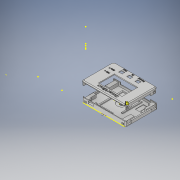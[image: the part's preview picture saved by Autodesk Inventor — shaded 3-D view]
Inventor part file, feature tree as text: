
AUTODESK INVENTOR PART (.ipt)
format: ipt  version: 2019 (Build 230136000, 136)  size: 3,585,536 bytes
history: native  units: mm
features: move_body x109, sketch x92, extrude x72, direct_edit x59, chamfer x6, other x3, split x1, draft x1, revolve x1, plane x1
ambient origin geometry x8: Origin, YZ Plane, XZ Plane, XY Plane, X Axis, Y Axis, Z Axis, Center Point
bodies: Solid1 (feature_tree), Solid2 (feature_tree), Solid3 (feature_tree)
feature tree (345):
  sketch  "Sketch1"  dims[d2=105.0mm d3=75.0mm d6=109.0mm]
  extrude  "Extrusion1"  Depth=109.0mm
  extrude  "Extrusion2"  Depth=79.0mm TaperAngle=0.0deg
  extrude  "Extrusion3"  Depth=2.5mm TaperAngle=0.0deg
  sketch  "Sketch6"  dims[d10=105.0mm d11=75.0mm d12=2.5mm d13=0.0mm]
  extrude  "Extrusion4"  Depth=19.5mm
  sketch  "Sketch8"  dims[d17=10.0mm d18=1.2mm d19=0.0mm]
  extrude  "Extrusion5"  Depth=10.0mm TaperAngle=0.0deg
  extrude  "Extrusion6"  Depth=30.0mm
  extrude  "Extrusion7"  Depth=60.0mm
  extrude  "Extrusion8"  Depth=1.0mm TaperAngle=0.0deg
  sketch  "Sketch14"  dims[d31=2.8mm d32=60.0mm]
  extrude  "Extrusion9"  Depth=20.0mm
  extrude  "Extrusion10"  Depth=0.5mm TaperAngle=0.0deg
  extrude  "Extrusion11"  Depth=12.5mm
  extrude  "Extrusion12"  Depth=10.0mm TaperAngle=0.0deg
  sketch  "Sketch17"  dims[d33=5.6mm d34=1.0mm d35=0.0mm]
  sketch  "Sketch18"  dims[d36=16.0mm d37=20.0mm]
  sketch  "Sketch19"  dims[d38=1.0mm d39=0.0mm d40=0.5mm d41=0.0mm]
  sketch  "Sketch20"  dims[d42=11.0mm d43=12.5mm]
  sketch  "Sketch21"  dims[d44=10.0mm d45=1.0mm d46=0.0mm]
  extrude  "Extrusion13"  Depth=2.0mm TaperAngle=0.0deg
  extrude  "Extrusion14"  Depth=15.0mm
  sketch  "Sketch22"  dims[d47=0.2mm d48=0.0mm d49=2.0mm d50=0.0mm]
  direct_edit  "Direct Edit1"
  direct_edit  "Direct Edit2"
  extrude  "Extrusion15"  Depth=70.0mm
  extrude  "Extrusion16"  Depth=58.0mm
  extrude  "Extrusion17"  Depth=2.0mm TaperAngle=0.0deg
  direct_edit  "Direct Edit3"
  direct_edit  "Direct Edit4"
  direct_edit  "Direct Edit5"
  extrude  "Extrusion18"  Depth=79.0mm
  extrude  "Extrusion19"  TaperAngle=0.0deg  [1 undecoded]
  extrude  "Extrusion20"  Depth=3.0mm TaperAngle=0.0deg
  extrude  "Extrusion21"  Depth=3.0mm
  direct_edit  "Direct Edit6"
  split  "Split1"
  move_body  "Move Body1"
  move_body  "Move Body2"
  move_body  "Move Body3"
  move_body  "Move Body4"
  move_body  "Move Body5"
  move_body  "Move Body6"
  sketch  "Sketch28"  dims[d63=2.5mm d64=0.0mm d65=0.0mm d66=0.0mm d67=-0.5mm]
  direct_edit  "Direct Edit7"
  sketch  "Sketch29"  dims[d68=0.0mm d69=0.0mm d70=1.0mm d71=3.0mm d72=0.0mm]
  extrude  "Extrusion22"  Depth=2.54mm
  extrude  "Extrusion23"  Depth=5.588mm
  sketch  "Sketch32"  dims[d84=11.176mm d85=5.588mm]
  direct_edit  "Direct Edit8"
  direct_edit  "Direct Edit9"
  extrude  "Extrusion24"  TaperAngle=0.0deg  [1 undecoded]
  direct_edit  "Direct Edit10"
  direct_edit  "Direct Edit11"
  direct_edit  "Direct Edit12"
  sketch  "Sketch33"  dims[d86=1.0mm d87=0.0mm d88=0.0mm d89=0.0mm d90=-47.25mm]
  direct_edit  "Direct Edit13"
  other  "Work Point1"
  sketch  "Sketch34"  dims[d91=0.0mm d92=0.0mm d93=-95.5mm d94=0.0mm d95=0.0mm d96=-0.6mm]
  other  "Work Point2"
  other  "Work Point3"
  sketch  "Sketch35"  dims[d101=27.7mm d102=48.2mm]
  extrude  "Extrusion25"  TaperAngle=0.0deg  [1 undecoded]
  extrude  "Extrusion26"  Depth=48.2mm
  direct_edit  "Direct Edit14"
  direct_edit  "Direct Edit15"
  extrude  "Extrusion27"  Depth=7.0mm
  extrude  "Extrusion28"  Depth=7.0mm
  direct_edit  "Direct Edit16"
  draft  "FaceDraft1"
  chamfer  "Chamfer1"  Distance=4.0mm
  chamfer  "Chamfer2"  Distance=3.0mm
  chamfer  "Chamfer3"  Distance=1.0mm
  direct_edit  "Direct Edit17"
  direct_edit  "Direct Edit18"
  extrude  "Extrusion29"  Depth=1.5mm TaperAngle=0.0deg
  extrude  "Extrusion30"  TaperAngle=0.0deg  [1 undecoded]
  extrude  "Extrusion31"  TaperAngle=180.0deg  [1 undecoded]
  sketch  "Sketch42"  dims[d121=9.75mm d122=12.75mm d123=244.0mm d124=-9.75mm d125=0.0mm d126=0.0mm]
  direct_edit  "Direct Edit19"
  sketch  "Sketch43"  dims[d127=180.0deg d128=180.0deg]
  direct_edit  "Direct Edit20"
  sketch  "Sketch44"  dims[d129=180.0deg d130=122.75mm d131=-19.25mm d132=0.0mm]
  extrude  "Extrusion32"  Depth=122.75mm TaperAngle=0.0deg
  direct_edit  "Direct Edit21"
  extrude  "Extrusion33"  Depth=5.0mm
  extrude  "Extrusion34"  Depth=5.0mm
  sketch  "Sketch48"  dims[d141=5.0mm d142=5.0mm]
  sketch  "Sketch49"  dims[d143=5.0mm d144=2.0mm]
  extrude  "Extrusion35"  Depth=5.0mm
  sketch  "Sketch51"  dims[d147=2.0mm d148=1.0mm d149=0.0mm]
  extrude  "Extrusion36"  Depth=5.0mm
  extrude  "Extrusion37"  Depth=2.0mm
  move_body  "Move Body7"
  move_body  "Move Body8"
  move_body  "Move Body9"
  move_body  "Move Body10"
  move_body  "Move Body11"
  move_body  "Move Body12"
  sketch  "Sketch53"  dims[d152=5.0mm d153=5.0mm]
  direct_edit  "Direct Edit22"
  extrude  "Extrusion38"  Depth=2.0mm
  sketch  "Sketch54"  dims[d154=5.0mm d155=5.0mm]
  sketch  "Sketch55"  dims[d156=5.0mm d157=5.0mm]
  sketch  "Sketch56"  dims[d158=3.0mm d159=3.0mm]
  extrude  "Extrusion39"  Depth=1.0mm TaperAngle=0.0deg
  direct_edit  "Direct Edit23"
  sketch  "Sketch58"  dims[d162=3.0mm d163=0.0mm d164=11.0mm]
  direct_edit  "Direct Edit24"
  extrude  "Extrusion40"  Depth=5.0mm
  direct_edit  "Direct Edit25"
  extrude  "Extrusion41"  Depth=5.0mm
  direct_edit  "Direct Edit26"
  direct_edit  "Direct Edit27"
  direct_edit  "Direct Edit28"
  direct_edit  "Direct Edit29"
  extrude  "Extrusion42"  Depth=5.0mm
  extrude  "Extrusion43"  Depth=5.0mm
  direct_edit  "Direct Edit30"
  sketch  "Sketch62"  dims[d171=11.0mm d172=0.0mm d173=0.0mm d174=1.0mm]
  extrude  "Extrusion44"  Depth=3.0mm
  direct_edit  "Direct Edit31"
  direct_edit  "Direct Edit32"
  extrude  "Extrusion45"  Depth=3.0mm
  move_body  "Move Body13"
  move_body  "Move Body14"
  move_body  "Move Body15"
  move_body  "Move Body16"
  extrude  "Extrusion46"  Depth=3.0mm
  sketch  "Sketch66"  dims[d192=0.0mm d193=0.0mm d194=1.0mm d195=12.5mm]
  direct_edit  "Direct Edit33"
  sketch  "Sketch67"  dims[d196=5.0mm d198=2.1mm]
  direct_edit  "Direct Edit34"
  extrude  "Extrusion47"  Depth=11.0mm
  direct_edit  "Direct Edit35"
  move_body  "Move Body17"
  direct_edit  "Direct Edit36"
  direct_edit  "Direct Edit37"
  direct_edit  "Direct Edit38"
  direct_edit  "Direct Edit39"
  direct_edit  "Direct Edit40"
  direct_edit  "Direct Edit41"
  extrude  "Extrusion48"  Depth=11.0mm
  extrude  "Extrusion49"  Depth=11.0mm
  extrude  "Extrusion50"  Depth=1.0mm TaperAngle=0.0deg
  sketch  "Sketch72"  dims[d213=5.0mm d214=0.0mm d215=0.6mm]
  revolve  "Revolution1"  [1 undecoded]
  sketch  "Sketch74"  dims[d218=5.0mm d219=0.0mm d220=0.0mm d221=0.0mm d222=-0.2mm]
  sketch  "Sketch75"  dims[d223=0.0mm d224=0.0mm d225=0.2mm d226=30.0deg]
  plane  "Work Plane1"
  extrude  "Extrusion51"  Depth=1.0mm TaperAngle=0.0deg
  direct_edit  "Direct Edit42"
  sketch  "Sketch77"  dims[d233=1.07845mm d234=2.0mm d235=45.0deg d236=0.0mm d237=0.0mm d238=-0.5mm]
  extrude  "Extrusion52"  TaperAngle=0.0deg  [1 undecoded]
  extrude  "Extrusion53"  Depth=12.5mm
  extrude  "Extrusion54"  Depth=2.1mm
  extrude  "Extrusion55"  Depth=10.0mm
  direct_edit  "Direct Edit43"
  direct_edit  "Direct Edit44"
  extrude  "Extrusion56"  TaperAngle=0.0deg  [1 undecoded]
  extrude  "Extrusion57"  Depth=0.6mm
  extrude  "Extrusion58"  Depth=3.05mm
  extrude  "Extrusion59"  Depth=0.6mm
  extrude  "Extrusion60"  Depth=13.7mm
  extrude  "Extrusion61"  TaperAngle=0.0deg  [1 undecoded]
  direct_edit  "Direct Edit45"
  direct_edit  "Direct Edit46"
  direct_edit  "Direct Edit47"
  extrude  "Extrusion62"  TaperAngle=30.0deg  [1 undecoded]
  direct_edit  "Direct Edit48"
  sketch  "Sketch89"  dims[d283=4.75mm d284=0.0mm d285=-118.0mm]
  extrude  "Extrusion63"  Depth=0.8mm TaperAngle=45.0deg
  extrude  "Extrusion64"  TaperAngle=0.0deg  [1 undecoded]
  extrude  "Extrusion65"  Depth=0.6mm TaperAngle=0.0deg
  extrude  "Extrusion66"  Depth=7.5mm
  extrude  "Extrusion67"  Depth=17.5mm
  sketch  "Sketch95"  dims[d299=17.8mm]
  sketch  "Sketch96"  dims[d300=20.6mm]
  extrude  "Extrusion68"  Depth=1.0mm TaperAngle=0.0deg
  direct_edit  "Direct Edit49"
  direct_edit  "Direct Edit50"
  direct_edit  "Direct Edit51"
  extrude  "Extrusion69"  Depth=3.0mm
  extrude  "Extrusion70"  Depth=1.2mm TaperAngle=0.0deg
  direct_edit  "Direct Edit52"
  extrude  "Extrusion71"  Depth=2.0mm TaperAngle=0.0deg
  direct_edit  "Direct Edit53"
  direct_edit  "Direct Edit54"
  sketch  "Sketch100"  dims[d307=13.0mm]
  extrude  "Extrusion72"  Depth=23.0mm
  direct_edit  "Direct Edit55"
  direct_edit  "Direct Edit56"
  direct_edit  "Direct Edit57"
  direct_edit  "Direct Edit58"
  direct_edit  "Direct Edit59"
  chamfer  "Chamfer4"  Distance=1.2mm
  chamfer  "Chamfer5"  Distance=1.0mm
  chamfer  "Chamfer6"  Distance=2.0mm
  sketch  "Sketch5"  dims[d7=79.0mm d8=7.0mm d9=0.0mm]
  sketch  "Sketch7"  dims[d14=5.0mm d15=0.0mm d16=19.5mm]
  sketch  "Sketch11"  dims[d28=1.0mm d29=0.0mm d30=30.0mm]
  sketch  "Sketch23"  dims[d51=2.0mm d52=0.0mm d53=15.0mm]
  sketch  "Sketch24"  dims[d54=9.0mm d55=70.0mm]
  sketch  "Sketch25"  dims[d56=46.5mm d57=58.0mm]
  sketch  "Sketch26"  dims[d58=39.0mm d59=2.0mm d60=0.0mm]
  sketch  "Sketch27"  dims[d61=109.0mm d62=79.0mm]
  sketch  "Sketch30"  dims[d73=1.0mm d74=0.0mm d79=3.0mm]
  sketch  "Sketch31"  dims[d82=4.5mm d83=2.54mm]
  sketch  "Sketch36"  dims[d103=68.2mm d104=7.0mm]
  sketch  "Sketch37"  dims[d105=5.5mm d106=7.0mm]
  sketch  "Sketch38"  dims[d107=5.5mm]
  sketch  "Sketch39"  dims[d108=7.0mm]
  sketch  "Sketch40"  dims[d109=5.5mm d110=4.0mm d111=0.0mm d112=3.0mm d113=0.0mm d114=1.0mm d115=0.0mm]
  sketch  "Sketch41"  dims[d116=1.0mm d117=0.0mm d118=0.0mm d119=0.0mm d120=1.5mm]
  sketch  "Sketch45"  dims[d133=0.0mm d134=0.0mm d135=-1.0mm d136=5.0mm]
  sketch  "Sketch46"  dims[d137=5.0mm d138=5.0mm]
  sketch  "Sketch47"  dims[d139=5.0mm d140=5.0mm]
  sketch  "Sketch50"  dims[d145=2.0mm d146=2.0mm]
  sketch  "Sketch52"  dims[d150=5.0mm d151=5.0mm]
  sketch  "Sketch57"  dims[d160=3.0mm d161=3.0mm]
  sketch  "Sketch59"  dims[d165=11.0mm d166=11.0mm]
  sketch  "Sketch60"  dims[d167=11.0mm d168=11.0mm]
  sketch  "Sketch61"  dims[d169=11.0mm d170=11.0mm]
  sketch  "Sketch63"  dims[d175=0.0mm d176=0.0mm d177=1.0mm d178=2.0mm d179=0.0mm]
  sketch  "Sketch64"  dims[d180=0.0mm d181=0.0mm d182=1.0mm d183=0.0mm d184=0.0mm d185=1.0mm]
  sketch  "Sketch65"  dims[d186=0.0mm d187=0.0mm d188=-5.0mm d189=-5.0mm d190=0.0mm d191=0.0mm]
  sketch  "Sketch68"  dims[d199=10.0mm d200=0.0mm d201=10.0mm]
  sketch  "Sketch69"  dims[d202=0.5mm d203=0.0mm d204=0.0mm d205=0.0mm d206=-0.75mm]
  sketch  "Sketch70"  dims[d207=0.0mm d208=0.0mm d209=2.75mm d210=0.6mm]
  sketch  "Sketch71"  dims[d211=3.05mm d212=13.7mm]
  sketch  "Sketch73"  dims[d216=2.7mm d217=13.7mm]
  sketch  "Sketch76"  dims[d227=1.0mm d228=2.0mm d229=45.0deg d230=0.8mm d231=2.0mm d232=45.0deg]
  sketch  "Sketch78"  dims[d239=0.0mm d240=0.0mm d241=-1.25mm d242=0.6mm d243=0.0mm]
  sketch  "Sketch79"  dims[d244=1.0mm d245=0.0mm d246=7.5mm]
  sketch  "Sketch80"  dims[d247=20.0mm d248=17.5mm]
  sketch  "Sketch81"  dims[d249=17.5mm d250=1.0mm d251=0.0mm]
  sketch  "Sketch82"  dims[d254=0.0mm d255=0.0mm d256=1.2mm d257=3.0mm]
  sketch  "Sketch83"  dims[d258=0.0mm d259=0.0mm d260=-2.0mm d261=1.2mm d262=0.0mm]
  sketch  "Sketch84"  dims[d263=0.0mm d264=0.0mm d265=-0.5mm d266=2.0mm d267=0.0mm]
  sketch  "Sketch85"  dims[d268=1.0mm d269=0.0mm d271=23.0mm]
  sketch  "Sketch86"  dims[d272=9.8mm d273=1.2mm d274=0.0mm]
  sketch  "Sketch87"  dims[d275=8.8mm d276=1.0mm d277=0.0mm d278=2.0mm d279=0.0mm]
  sketch  "Sketch88"  dims[d280=2.0mm d281=0.0mm d282=-117.25mm]
  sketch  "Sketch90"  dims[d286=163.5mm d287=0.0mm d288=79.0mm]
  sketch  "Sketch91"  dims[d289=-132.0mm d290=0.0mm d291=2.0mm]
  sketch  "Sketch92"  dims[d292=165.25mm d293=0.0mm d294=78.0mm]
  sketch  "Sketch93"  dims[d295=0.0mm d296=8.5mm d297=0.0mm]
  sketch  "Sketch94"  dims[d298=3.7mm]
  sketch  "Sketch97"  dims[d301=35.6mm]
  sketch  "Sketch98"  dims[d302=0.0mm d303=0.0mm d304=0.75mm]
  sketch  "Sketch99"  dims[d305=1.0mm d306=0.0mm]
  sketch  "Sketch101"  dims[d308=12.0mm d309=180.0deg d310=1.0mm d311=0.0mm d312=0.0mm d313=0.0mm d314=-1.0mm d315=15.0mm d316=15.0mm d317=15.0mm d318=15.0mm d319=15.0mm d320=15.0mm d321=15.0mm d322=13.0mm d323=0.0mm d324=0.0mm d325=2.25mm d326=0.0mm d327=0.0mm d328=2.0mm d329=0.0mm d330=0.0mm d331=2.0mm d332=4.5mm d333=0.0mm d334=0.0mm d335=0.0mm d336=2.5mm d337=0.0mm d338=0.0mm d339=2.5mm d340=2.0mm d341=0.0mm d342=0.0mm d343=0.0mm d344=54.0mm d345=0.0mm d346=0.0mm d347=0.25mm d348=0.0mm d349=0.0mm d350=-0.25mm d351=0.0mm d352=0.0mm d353=2.75mm d354=0.0mm d355=0.0mm d356=-0.01583mm d357=4.0mm d358=0.0mm d359=15.3mm d360=15.3mm d361=13.3mm d362=15.3mm d363=13.3mm d364=15.3mm d365=13.3mm d366=4.5mm d367=0.0mm d368=0.0mm d369=0.0mm d370=-2.1mm d371=4.5mm d372=0.0mm d373=0.0mm d374=0.0mm d375=-2.4mm d376=0.0mm d377=0.0mm d378=-0.25mm d379=0.0mm d380=0.0mm d381=2.5mm d382=0.0mm d383=0.0mm d384=1.25mm d385=6.0mm d386=6.0mm d387=6.0mm d388=6.0mm d389=1.0mm d390=0.0mm d391=180.0deg d392=180.0deg d393=99.75mm d394=0.0mm d395=-79.25mm d396=0.0mm d397=-6.0mm d398=0.0mm d399=0.6mm d400=0.0mm d401=0.0mm d402=5.0mm d403=0.0mm d404=0.0mm d405=0.0mm d406=1.0mm d407=25.2mm d408=20.6mm d409=1.0mm d410=0.0mm d411=0.0mm d412=0.0mm d413=0.5mm d414=0.0mm d415=33.75mm d416=1.25mm d417=0.0mm d418=0.0mm d419=-0.3mm d420=0.0mm d421=0.0mm d422=-0.3mm d423=0.0mm d424=0.0mm d425=-0.3mm d426=0.0mm d427=0.0mm d428=-0.3mm d429=0.0mm d430=0.0mm d431=-0.3mm d432=0.0mm d433=0.0mm d434=-0.3mm d435=0.0mm d436=0.0mm d437=-0.3mm d438=0.0mm d439=0.0mm d440=-0.3mm d441=0.0mm d442=0.0mm d443=-0.5mm d444=0.0mm d445=0.0mm d446=-0.3mm d447=0.0mm d448=0.0mm d449=-0.3mm d450=0.0mm d451=0.0mm d452=-0.3mm d453=0.0mm d454=0.0mm d455=-0.3mm d456=0.0mm d457=0.0mm d458=-0.5mm d459=0.0mm d460=0.0mm d461=-1.0mm d462=0.0mm d463=0.0mm d464=-1.5mm d465=0.0mm d466=0.0mm d467=0.3mm d468=2.0mm d469=1.0mm d470=0.0mm d471=0.6mm d472=0.0mm d473=0.6mm d474=0.0mm d475=4.5mm d476=4.0mm d477=45.0deg d478=-4.5mm d479=5.0mm d480=5.0mm d481=3.0mm d482=0.0mm d483=0.0mm d484=0.0mm d485=-16.5mm d486=3.75mm d487=0.0mm d488=8.0mm d489=0.0mm d490=8.0mm d491=8.0mm d492=8.0mm d493=8.0mm d494=9.0mm d495=9.0mm d496=9.0mm d497=9.0mm d498=8.0mm d499=0.0mm d500=8.0mm d501=1.0mm d502=8.0mm d503=1.0mm d504=8.0mm d505=1.4mm d506=1.0mm d507=8.0mm d508=1.0mm d509=8.0mm d510=0.0mm d511=0.0mm d512=0.0mm d513=-0.2mm d514=0.0mm d515=0.0mm d516=-0.2mm d517=0.0mm d518=0.0mm d519=-1.2mm d520=3.0mm d521=3.0mm d522=2.0mm d523=0.0mm d524=1.5mm d525=1.5mm d526=3.0mm d527=0.0mm d528=1.0mm d529=1.0mm d530=3.0mm d531=0.0mm d532=3.0mm d533=3.0mm d534=2.0mm d535=0.0mm d536=1.5mm d537=1.5mm d538=3.0mm d539=0.0mm d540=1.0mm d541=1.0mm d542=3.0mm d543=0.0mm d544=0.0mm d545=0.0mm d546=0.05mm d547=0.0mm d548=0.0mm d549=0.05mm d550=0.0mm d551=0.0mm d552=1.25mm d553=3.0mm d554=3.0mm d555=111.0mm d556=0.0mm d557=0.0mm d558=0.0mm d559=-0.2mm d560=0.0mm d561=0.0mm d562=-0.2mm d563=3.5mm d564=0.0mm d565=3.5mm d566=0.0mm d567=5.0mm d568=0.0mm d569=5.0mm d570=0.0mm d571=2.2mm d572=2.2mm d573=3.0mm d574=0.0mm d575=2.2mm d576=2.2mm d577=3.0mm d578=0.0mm d579=0.0mm d580=0.0mm d581=3.8mm d582=0.0mm d583=0.0mm d584=-3.35mm d585=0.0mm d586=0.0mm d587=-3.35mm d588=0.0mm d589=0.0mm d590=3.8mm d591=0.0mm d592=0.0mm d593=1.5mm d594=0.0mm d595=0.0mm d596=1.5mm d597=0.0mm d598=0.0mm d599=1.5mm d600=0.0mm d601=0.0mm d602=1.5mm d603=6.0mm d604=6.0mm d605=1.5mm d606=0.0mm d607=6.0mm d608=6.0mm d609=1.5mm d610=0.0mm d611=0.0mm d612=0.0mm d613=14.0mm d614=14.0mm d615=0.0mm d616=0.0mm d617=0.0mm d618=14.0mm d619=0.0mm d620=0.0mm d621=14.0mm d622=0.0mm d623=0.0mm d624=-0.75mm d625=14.0mm d626=2.0mm d627=0.0mm d628=0.0mm d629=0.0mm d630=-0.25mm d631=0.0mm d632=0.0mm d633=-0.25mm d634=-0.5mm d635=0.0mm d636=0.0mm d637=0.0mm d638=0.0mm d639=-0.25mm d640=0.0mm d641=0.0mm d642=-0.25mm d643=0.0mm d644=0.0mm d645=-0.25mm d646=0.0mm d647=0.0mm d648=-0.25mm d649=0.0mm d650=0.0mm d651=-0.25mm d652=0.0mm d653=0.0mm d654=-0.25mm d655=0.0mm d656=0.0mm d657=-0.25mm d658=0.0mm d659=0.0mm d660=-0.5mm d661=2.0mm d662=2.0mm d663=45.0deg d664=2.0mm d665=2.0mm d666=45.0deg d667=2.0mm d668=2.0mm d669=45.0deg]
  move_body  "Move1"
  move_body  "Move2"
  move_body  "Move3"
  move_body  "Move4"
  move_body  "Move5"
  move_body  "Move6"
  move_body  "Move7"
  move_body  "Move8"
  move_body  "Move9"
  move_body  "Move10"
  move_body  "Move11"
  move_body  "Move12"
  move_body  "Move13"
  move_body  "Move14"
  move_body  "Move15"
  move_body  "Move16"
  move_body  "Move17"
  move_body  "Move18"
  move_body  "Move19"
  move_body  "Move20"
  move_body  "Move21"
  move_body  "Move22"
  move_body  "Move23"
  move_body  "Move24"
  move_body  "Move25"
  move_body  "Move26"
  move_body  "Move27"
  move_body  "Move28"
  move_body  "Move29"
  move_body  "Move30"
  move_body  "Move31"
  move_body  "Move32"
  move_body  "Move33"
  move_body  "Move34"
  move_body  "Move35"
  move_body  "Move36"
  move_body  "Move37"
  move_body  "Move38"
  move_body  "Move39"
  move_body  "Move40"
  move_body  "Move41"
  move_body  "Move42"
  move_body  "Move43"
  move_body  "Move44"
  move_body  "Move45"
  move_body  "Move46"
  move_body  "Move47"
  move_body  "Move48"
  move_body  "Move49"
  move_body  "Move50"
  move_body  "Move51"
  move_body  "Move52"
  move_body  "Move53"
  move_body  "Move54"
  move_body  "Move55"
  move_body  "Move56"
  move_body  "Move57"
  move_body  "Move58"
  move_body  "Move59"
  move_body  "Move60"
  move_body  "Move61"
  move_body  "Move62"
  move_body  "Move63"
  move_body  "Move64"
  move_body  "Move65"
  move_body  "Move66"
  move_body  "Move67"
  move_body  "Move68"
  move_body  "Move69"
  move_body  "Move70"
  move_body  "Move71"
  move_body  "Move72"
  move_body  "Move73"
  move_body  "Move74"
  move_body  "Move75"
  move_body  "Move76"
  move_body  "Move77"
  move_body  "Move78"
  move_body  "Move79"
  move_body  "Move80"
  move_body  "Move81"
  move_body  "Move82"
  move_body  "Move83"
  move_body  "Move84"
  move_body  "Move85"
  move_body  "Move86"
  move_body  "Move87"
  move_body  "Move88"
  move_body  "Move89"
  move_body  "Move90"
  move_body  "Move91"
  move_body  "Move92"
note: 11 required parameter values undecoded (feature->parameter linkage not recoverable at this tier; creation-order binding heuristic only, values carry confidence <= 0.55)